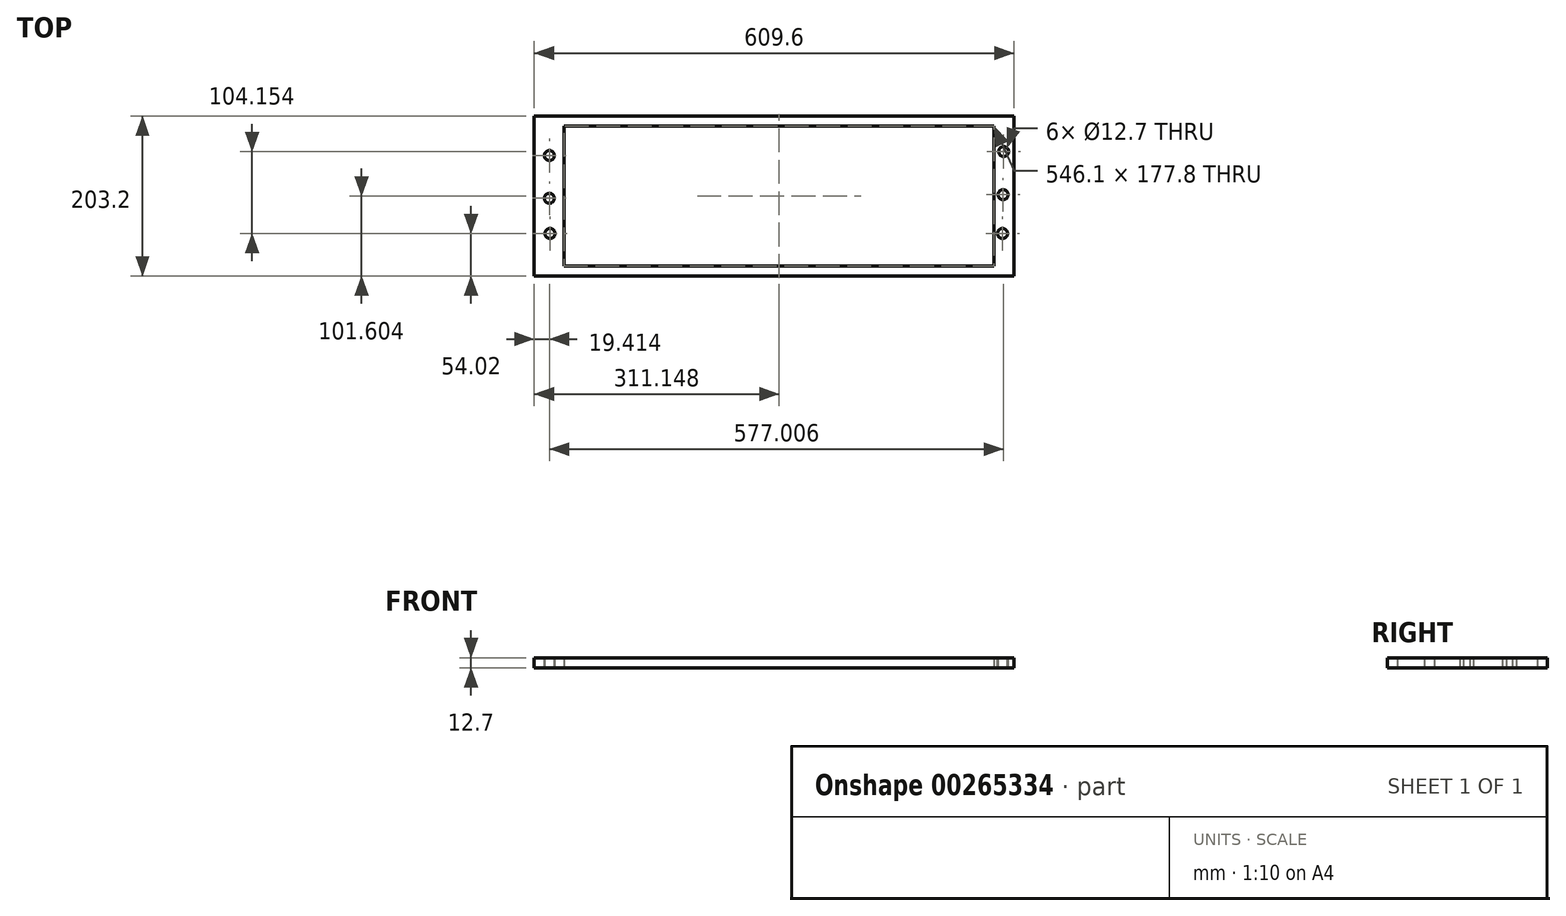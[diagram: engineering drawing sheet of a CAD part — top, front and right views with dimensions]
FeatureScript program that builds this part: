
annotation { "Feature Type Name" : "Feature", "Feature Type Description" : "" }
export const myFeature = defineFeature(function(context is Context, id is Id, definition is map)
    precondition{}
    {
        {
            var Q0;
            Q0=qCreatedBy(makeId("Top.planeOp"),FACE);
            var sketch = newSketch(context, id + "F0", { "sketchPlane" : qUnion([Q0])});
            skLineSegment(sketch, "E0.bottom", {"start": v(-240.44, 149.18) * mm, "end": v(369.16, 149.18) * mm});
            skLineSegment(sketch, "E0.top", {"start": v(-240.44, -54.02) * mm, "end": v(369.16, -54.02) * mm});
            skLineSegment(sketch, "E0.left", {"start": v(-240.44, 149.18) * mm, "end": v(-240.44, -54.02) * mm});
            skLineSegment(sketch, "E0.right", {"start": v(369.16, 149.18) * mm, "end": v(369.16, -54.02) * mm});
            skLineSegment(sketch, "E1.bottom", {"start": v(-202.34, 136.48) * mm, "end": v(343.76, 136.48) * mm});
            skLineSegment(sketch, "E1.top", {"start": v(-202.34, -41.32) * mm, "end": v(343.76, -41.32) * mm});
            skLineSegment(sketch, "E1.left", {"start": v(-202.34, 136.48) * mm, "end": v(-202.34, -41.32) * mm});
            skLineSegment(sketch, "E1.right", {"start": v(343.76, 136.48) * mm, "end": v(343.76, -41.32) * mm});
            skSolve(sketch);
        }
        {
            var Q0;
            Q0=qSketchRegion(id+"F0",true);
            extrude(context, id + "F1", {"entities" : qUnion([Q0]), "endBound" : BoundingType.SYMMETRIC, "depth" : 12.7 * mm});
        }
        {
            var Q0;
            Q0=makeQuery(id+"F1.opExtrude","CAP_FACE",FACE,{"disambiguationData":[OSD([sQuery(id+"F0.wireOp",EDGE,"E0.bottom"),sQuery(id+"F0.wireOp",EDGE,"E0.top"),sQuery(id+"F0.wireOp",EDGE,"E0.left"),sQuery(id+"F0.wireOp",EDGE,"E0.right"),sQuery(id+"F0.wireOp",EDGE,"E1.bottom"),sQuery(id+"F0.wireOp",EDGE,"E1.top"),sQuery(id+"F0.wireOp",EDGE,"E1.left"),sQuery(id+"F0.wireOp",EDGE,"E1.right")])],"isStart":false});
            var sketch = newSketch(context, id + "F2", { "sketchPlane" : qUnion([Q0])});
            skPoint(sketch, "E2", {"position": v(-221.03, 99.04) * mm});
            skPoint(sketch, "E3", {"position": v(-221.03, 44.78) * mm});
            skPoint(sketch, "E4", {"position": v(-220.22, 0) * mm});
            skSolve(sketch);
        }
        {
            var Q0;
            Q0=sQuery(id+"F2.wireOp",VERTEX,"E2");
            var Q1;
            Q1=sQuery(id+"F2.wireOp",VERTEX,"E3");
            var Q2;
            Q2=sQuery(id+"F2.wireOp",VERTEX,"E4");
            var Q3;
            Q3=makeQuery(id+"F1.opExtrude","SWEPT_BODY",BODY,{"disambiguationData":[OSD([sQuery(id+"F0.wireOp",EDGE,"E0.bottom"),sQuery(id+"F0.wireOp",EDGE,"E0.top"),sQuery(id+"F0.wireOp",EDGE,"E0.left"),sQuery(id+"F0.wireOp",EDGE,"E0.right"),sQuery(id+"F0.wireOp",EDGE,"E1.bottom"),sQuery(id+"F0.wireOp",EDGE,"E1.top"),sQuery(id+"F0.wireOp",EDGE,"E1.left"),sQuery(id+"F0.wireOp",EDGE,"E1.right")])]});
            hole(context, id + "F3", {"style" : HoleStyle.SIMPLE, "endStyle" : HoleEndStyle.THROUGH, "holeDiameter" : 12.7 * mm, "tappedDepth" : 12.7 * mm, "tapClearance" : 3, "locations" : qUnion([Q0, Q1, Q2]), "scope" : qUnion([Q3])});
        }
        {
            var Q0;
            Q0=makeQuery(id+"F1.opExtrude","CAP_FACE",FACE,{"disambiguationData":[OSD([sQuery(id+"F0.wireOp",EDGE,"E0.bottom"),sQuery(id+"F0.wireOp",EDGE,"E0.top"),sQuery(id+"F0.wireOp",EDGE,"E0.left"),sQuery(id+"F0.wireOp",EDGE,"E0.right"),sQuery(id+"F0.wireOp",EDGE,"E1.bottom"),sQuery(id+"F0.wireOp",EDGE,"E1.top"),sQuery(id+"F0.wireOp",EDGE,"E1.left"),sQuery(id+"F0.wireOp",EDGE,"E1.right")])],"isStart":false});
            var sketch = newSketch(context, id + "F4", { "sketchPlane" : qUnion([Q0])});
            skPoint(sketch, "E5", {"position": v(355.3, 49.35) * mm});
            skPoint(sketch, "E6", {"position": v(355.98, 104.15) * mm});
            skPoint(sketch, "E7", {"position": v(354.63, 0) * mm});
            skSolve(sketch);
        }
        {
            var Q0;
            Q0=sQuery(id+"F4.wireOp",VERTEX,"E6");
            var Q1;
            Q1=sQuery(id+"F4.wireOp",VERTEX,"E5");
            var Q2;
            Q2=sQuery(id+"F4.wireOp",VERTEX,"E7");
            var Q3;
            Q3=makeQuery(id+"F1.opExtrude","SWEPT_BODY",BODY,{"disambiguationData":[OSD([sQuery(id+"F0.wireOp",EDGE,"E0.bottom"),sQuery(id+"F0.wireOp",EDGE,"E0.top"),sQuery(id+"F0.wireOp",EDGE,"E0.left"),sQuery(id+"F0.wireOp",EDGE,"E0.right"),sQuery(id+"F0.wireOp",EDGE,"E1.bottom"),sQuery(id+"F0.wireOp",EDGE,"E1.top"),sQuery(id+"F0.wireOp",EDGE,"E1.left"),sQuery(id+"F0.wireOp",EDGE,"E1.right")])]});
            hole(context, id + "F5", {"style" : HoleStyle.SIMPLE, "endStyle" : HoleEndStyle.THROUGH, "holeDiameter" : 12.7 * mm, "tappedDepth" : 12.7 * mm, "tapClearance" : 3, "locations" : qUnion([Q0, Q1, Q2]), "scope" : qUnion([Q3])});
        }
    });
